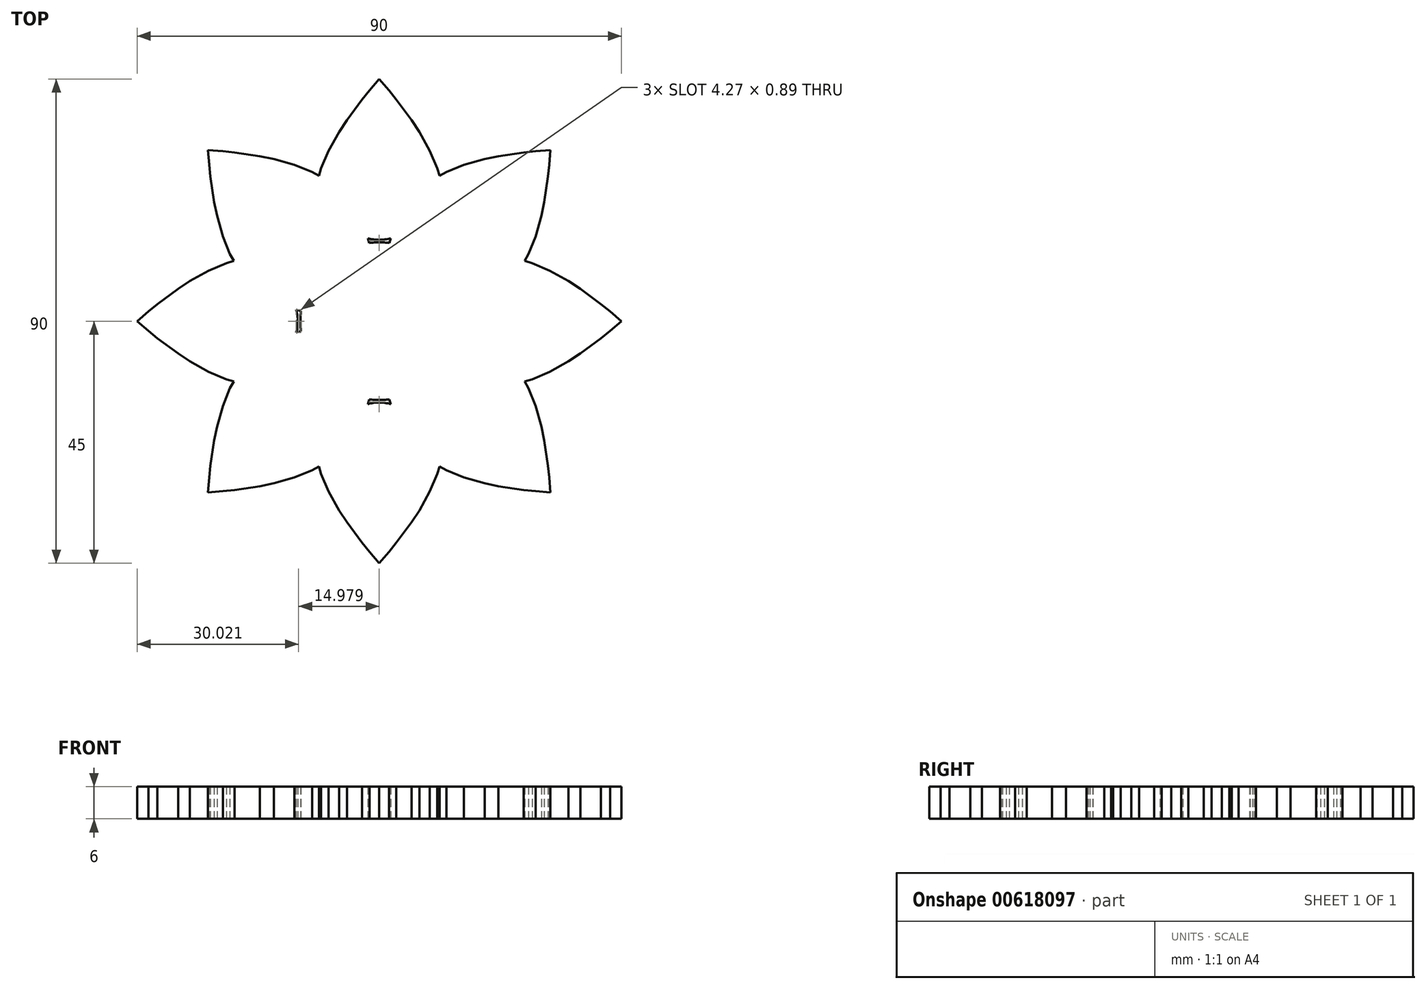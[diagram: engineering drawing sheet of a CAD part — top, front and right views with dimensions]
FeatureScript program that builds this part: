
annotation { "Feature Type Name" : "Feature", "Feature Type Description" : "" }
export const myFeature = defineFeature(function(context is Context, id is Id, definition is map)
    precondition{}
    {
        {
            var Q0;
            Q0=qCreatedBy(makeId("Top.planeOp"),FACE);
            var sketch = newSketch(context, id + "F0", { "sketchPlane" : qUnion([Q0])});
            skCircle(sketch, "E0", {"center": v(0, 0) * mm, "radius": 11.12 * mm});
            skCircle(sketch, "E1", {"center": v(22.72, 0) * mm, "radius": 7.6 * mm});
            skLineSegment(sketch, "E2", {"start": v(0, 0) * mm, "end": v(45, 0) * mm, "construction": true});
            skLineSegment(sketch, "E3", {"start": v(0, 0) * mm, "end": v(29.88, 51.75) * mm, "construction": true});
            skLineSegment(sketch, "E4", {"start": v(0, 0) * mm, "end": v(4, 3.29) * mm});
            skLineSegment(sketch, "E5", {"start": v(4, 3.29) * mm, "end": v(8.68, 6.96) * mm});
            skLineSegment(sketch, "E6", {"start": v(8.68, 6.96) * mm, "end": v(11.6, 8.96) * mm});
            skLineSegment(sketch, "E7", {"start": v(11.6, 8.96) * mm, "end": v(15.02, 10.78) * mm});
            skLineSegment(sketch, "E8", {"start": v(21.03, 12.1) * mm, "end": v(25.39, 11.67) * mm});
            skLineSegment(sketch, "E9", {"start": v(25.39, 11.67) * mm, "end": v(28.43, 10.8) * mm});
            skLineSegment(sketch, "E10", {"start": v(28.43, 10.8) * mm, "end": v(31.67, 9.4) * mm});
            skLineSegment(sketch, "E11", {"start": v(31.67, 9.4) * mm, "end": v(35.17, 7.45) * mm});
            skLineSegment(sketch, "E12", {"start": v(35.17, 7.45) * mm, "end": v(37.37, 6.01) * mm});
            skLineSegment(sketch, "E13", {"start": v(37.37, 6.01) * mm, "end": v(41.2, 3.18) * mm});
            skLineSegment(sketch, "E14", {"start": v(41.2, 3.18) * mm, "end": v(42.9, 1.8) * mm});
            skLineSegment(sketch, "E15", {"start": v(42.9, 1.8) * mm, "end": v(45, 0) * mm});
            skLineSegment(sketch, "E16", {"start": v(15.02, 10.78) * mm, "end": v(17.56, 11.63) * mm});
            skLineSegment(sketch, "E17", {"start": v(17.56, 11.63) * mm, "end": v(21.03, 12.1) * mm});
            skLineSegment(sketch, "E18.MirrorCS", {"start": v(11.6, -8.96) * mm, "end": v(15.02, -10.78) * mm});
            skLineSegment(sketch, "E19.MirrorCS", {"start": v(25.39, -11.67) * mm, "end": v(28.43, -10.8) * mm});
            skLineSegment(sketch, "E20.MirrorCS", {"start": v(8.68, -6.96) * mm, "end": v(11.6, -8.96) * mm});
            skLineSegment(sketch, "E21.MirrorCS", {"start": v(31.67, -9.4) * mm, "end": v(35.17, -7.45) * mm});
            skLineSegment(sketch, "E22.MirrorCS", {"start": v(41.2, -3.18) * mm, "end": v(42.9, -1.8) * mm});
            skLineSegment(sketch, "E23.MirrorCS", {"start": v(15.02, -10.78) * mm, "end": v(17.56, -11.63) * mm});
            skLineSegment(sketch, "E24.MirrorCS", {"start": v(17.56, -11.63) * mm, "end": v(21.03, -12.1) * mm});
            skLineSegment(sketch, "E25.MirrorCS", {"start": v(35.17, -7.45) * mm, "end": v(37.37, -6.01) * mm});
            skLineSegment(sketch, "E26.MirrorCS", {"start": v(42.9, -1.8) * mm, "end": v(45, 0) * mm});
            skLineSegment(sketch, "E27.MirrorCS", {"start": v(28.43, -10.8) * mm, "end": v(31.67, -9.4) * mm});
            skLineSegment(sketch, "E28.MirrorCS", {"start": v(4, -3.29) * mm, "end": v(8.68, -6.96) * mm});
            skLineSegment(sketch, "E29.MirrorCS", {"start": v(37.37, -6.01) * mm, "end": v(41.2, -3.18) * mm});
            skLineSegment(sketch, "E30.MirrorCS", {"start": v(21.03, -12.1) * mm, "end": v(25.39, -11.67) * mm});
            skLineSegment(sketch, "E31.MirrorCS", {"start": v(0, 0) * mm, "end": v(4, -3.29) * mm});
            skCircle(sketch, "E32", {"center": v(0, 0) * mm, "radius": 14.65 * mm});
            skLineSegment(sketch, "E33.1.0", {"start": v(0, 0) * mm, "end": v(31.82, 31.82) * mm, "construction": true});
            skCircle(sketch, "E33.1.2", {"center": v(16.07, 16.07) * mm, "radius": 7.6 * mm});
            skLineSegment(sketch, "E33.1.3", {"start": v(0, 0) * mm, "end": v(0.5, 5.15) * mm});
            skLineSegment(sketch, "E33.1.4", {"start": v(30.68, 22.17) * mm, "end": v(31.38, 26.88) * mm});
            skLineSegment(sketch, "E33.1.5", {"start": v(5.15, 0.5) * mm, "end": v(11.06, 1.22) * mm});
            skLineSegment(sketch, "E33.1.6", {"start": v(0.5, 5.15) * mm, "end": v(1.22, 11.06) * mm});
            skLineSegment(sketch, "E33.1.7", {"start": v(0, 0) * mm, "end": v(5.15, 0.5) * mm});
            skLineSegment(sketch, "E33.1.8", {"start": v(6.31, 23.43) * mm, "end": v(9.7, 26.2) * mm});
            skLineSegment(sketch, "E33.1.10", {"start": v(23.43, 6.31) * mm, "end": v(26.2, 9.7) * mm});
            skCircle(sketch, "E33.1.11", {"center": v(16.07, 16.07) * mm, "radius": 7.6 * mm});
            skLineSegment(sketch, "E33.1.12", {"start": v(0, 0) * mm, "end": v(31.82, 31.82) * mm, "construction": true});
            skLineSegment(sketch, "E33.1.14", {"start": v(20.65, 4.2) * mm, "end": v(23.43, 6.31) * mm});
            skLineSegment(sketch, "E33.1.15", {"start": v(12.47, 27.73) * mm, "end": v(15.75, 29.04) * mm});
            skLineSegment(sketch, "E33.1.16", {"start": v(3, 18.24) * mm, "end": v(4.2, 20.65) * mm});
            skLineSegment(sketch, "E33.1.17", {"start": v(4.2, 20.65) * mm, "end": v(6.31, 23.43) * mm});
            skLineSegment(sketch, "E33.1.18", {"start": v(29.04, 15.75) * mm, "end": v(30.14, 19.6) * mm});
            skLineSegment(sketch, "E33.1.19", {"start": v(31.6, 29.06) * mm, "end": v(31.82, 31.82) * mm});
            skLineSegment(sketch, "E33.1.20", {"start": v(15.75, 29.04) * mm, "end": v(19.6, 30.14) * mm});
            skLineSegment(sketch, "E33.1.21", {"start": v(30.14, 19.6) * mm, "end": v(30.68, 22.17) * mm});
            skLineSegment(sketch, "E33.1.22", {"start": v(1.86, 14.53) * mm, "end": v(3, 18.24) * mm});
            skCircle(sketch, "E33.1.23", {"center": v(16.07, 16.07) * mm, "radius": 7.6 * mm});
            skLineSegment(sketch, "E33.1.24", {"start": v(22.17, 30.68) * mm, "end": v(26.88, 31.38) * mm});
            skLineSegment(sketch, "E33.1.25", {"start": v(31.38, 26.88) * mm, "end": v(31.6, 29.06) * mm});
            skLineSegment(sketch, "E33.1.26", {"start": v(19.6, 30.14) * mm, "end": v(22.17, 30.68) * mm});
            skLineSegment(sketch, "E33.1.27", {"start": v(18.24, 3) * mm, "end": v(20.65, 4.2) * mm});
            skLineSegment(sketch, "E33.1.28", {"start": v(11.06, 1.22) * mm, "end": v(14.53, 1.86) * mm});
            skLineSegment(sketch, "E33.1.29", {"start": v(14.53, 1.86) * mm, "end": v(18.24, 3) * mm});
            skLineSegment(sketch, "E33.1.30", {"start": v(0, 0) * mm, "end": v(31.82, 31.82) * mm, "construction": true});
            skLineSegment(sketch, "E33.1.31", {"start": v(1.22, 11.06) * mm, "end": v(1.86, 14.53) * mm});
            skLineSegment(sketch, "E33.1.32", {"start": v(27.73, 12.47) * mm, "end": v(29.04, 15.75) * mm});
            skLineSegment(sketch, "E33.1.33", {"start": v(9.7, 26.2) * mm, "end": v(12.47, 27.73) * mm});
            skLineSegment(sketch, "E33.1.34", {"start": v(26.88, 31.38) * mm, "end": v(29.06, 31.6) * mm});
            skLineSegment(sketch, "E33.1.35", {"start": v(26.2, 9.7) * mm, "end": v(27.73, 12.47) * mm});
            skLineSegment(sketch, "E33.1.36", {"start": v(29.06, 31.6) * mm, "end": v(31.82, 31.82) * mm});
            skCircle(sketch, "E33.1.37", {"center": v(16.07, 16.07) * mm, "radius": 7.6 * mm});
            skLineSegment(sketch, "E33.1.38", {"start": v(0, 0) * mm, "end": v(31.82, 31.82) * mm, "construction": true});
            skLineSegment(sketch, "E33.2.0", {"start": v(0, 0) * mm, "end": v(0, 45) * mm, "construction": true});
            skCircle(sketch, "E33.2.2", {"center": v(0, 22.72) * mm, "radius": 7.6 * mm});
            skLineSegment(sketch, "E33.2.3", {"start": v(0, 0) * mm, "end": v(-3.29, 4) * mm});
            skLineSegment(sketch, "E33.2.4", {"start": v(6.01, 37.37) * mm, "end": v(3.18, 41.2) * mm});
            skLineSegment(sketch, "E33.2.5", {"start": v(3.29, 4) * mm, "end": v(6.96, 8.68) * mm});
            skLineSegment(sketch, "E33.2.6", {"start": v(-3.29, 4) * mm, "end": v(-6.96, 8.68) * mm});
            skLineSegment(sketch, "E33.2.7", {"start": v(0, 0) * mm, "end": v(3.29, 4) * mm});
            skLineSegment(sketch, "E33.2.8", {"start": v(-12.1, 21.03) * mm, "end": v(-11.67, 25.39) * mm});
            skLineSegment(sketch, "E33.2.10", {"start": v(12.1, 21.03) * mm, "end": v(11.67, 25.39) * mm});
            skCircle(sketch, "E33.2.11", {"center": v(0, 22.72) * mm, "radius": 7.6 * mm});
            skLineSegment(sketch, "E33.2.12", {"start": v(0, 0) * mm, "end": v(0, 45) * mm, "construction": true});
            skLineSegment(sketch, "E33.2.14", {"start": v(11.63, 17.56) * mm, "end": v(12.1, 21.03) * mm});
            skLineSegment(sketch, "E33.2.15", {"start": v(-10.8, 28.43) * mm, "end": v(-9.4, 31.67) * mm});
            skLineSegment(sketch, "E33.2.16", {"start": v(-10.78, 15.02) * mm, "end": v(-11.63, 17.56) * mm});
            skLineSegment(sketch, "E33.2.17", {"start": v(-11.63, 17.56) * mm, "end": v(-12.1, 21.03) * mm});
            skLineSegment(sketch, "E33.2.18", {"start": v(9.4, 31.67) * mm, "end": v(7.45, 35.17) * mm});
            skLineSegment(sketch, "E33.2.19", {"start": v(1.8, 42.9) * mm, "end": v(0, 45) * mm});
            skLineSegment(sketch, "E33.2.20", {"start": v(-9.4, 31.67) * mm, "end": v(-7.45, 35.17) * mm});
            skLineSegment(sketch, "E33.2.21", {"start": v(7.45, 35.17) * mm, "end": v(6.01, 37.37) * mm});
            skLineSegment(sketch, "E33.2.22", {"start": v(-8.96, 11.6) * mm, "end": v(-10.78, 15.02) * mm});
            skCircle(sketch, "E33.2.23", {"center": v(0, 22.72) * mm, "radius": 7.6 * mm});
            skLineSegment(sketch, "E33.2.24", {"start": v(-6.01, 37.37) * mm, "end": v(-3.18, 41.2) * mm});
            skLineSegment(sketch, "E33.2.25", {"start": v(3.18, 41.2) * mm, "end": v(1.8, 42.9) * mm});
            skLineSegment(sketch, "E33.2.26", {"start": v(-7.45, 35.17) * mm, "end": v(-6.01, 37.37) * mm});
            skLineSegment(sketch, "E33.2.27", {"start": v(10.78, 15.02) * mm, "end": v(11.63, 17.56) * mm});
            skLineSegment(sketch, "E33.2.28", {"start": v(6.96, 8.68) * mm, "end": v(8.96, 11.6) * mm});
            skLineSegment(sketch, "E33.2.29", {"start": v(8.96, 11.6) * mm, "end": v(10.78, 15.02) * mm});
            skLineSegment(sketch, "E33.2.30", {"start": v(0, 0) * mm, "end": v(0, 45) * mm, "construction": true});
            skLineSegment(sketch, "E33.2.31", {"start": v(-6.96, 8.68) * mm, "end": v(-8.96, 11.6) * mm});
            skLineSegment(sketch, "E33.2.32", {"start": v(10.8, 28.43) * mm, "end": v(9.4, 31.67) * mm});
            skLineSegment(sketch, "E33.2.33", {"start": v(-11.67, 25.39) * mm, "end": v(-10.8, 28.43) * mm});
            skLineSegment(sketch, "E33.2.34", {"start": v(-3.18, 41.2) * mm, "end": v(-1.8, 42.9) * mm});
            skLineSegment(sketch, "E33.2.35", {"start": v(11.67, 25.39) * mm, "end": v(10.8, 28.43) * mm});
            skLineSegment(sketch, "E33.2.36", {"start": v(-1.8, 42.9) * mm, "end": v(0, 45) * mm});
            skCircle(sketch, "E33.2.37", {"center": v(0, 22.72) * mm, "radius": 7.6 * mm});
            skLineSegment(sketch, "E33.2.38", {"start": v(0, 0) * mm, "end": v(0, 45) * mm, "construction": true});
            skCircle(sketch, "E34.5.3.0", {"center": v(-16.07, 16.07) * mm, "radius": 7.6 * mm});
            skLineSegment(sketch, "E34.7.3.0", {"start": v(0, 0) * mm, "end": v(-5.15, 0.5) * mm});
            skLineSegment(sketch, "E34.10.3.0", {"start": v(-22.17, 30.68) * mm, "end": v(-26.88, 31.38) * mm});
            skLineSegment(sketch, "E34.13.3.0", {"start": v(-0.5, 5.15) * mm, "end": v(-1.22, 11.06) * mm});
            skLineSegment(sketch, "E34.14.3.0", {"start": v(0, 0) * mm, "end": v(-31.82, 31.82) * mm, "construction": true});
            skLineSegment(sketch, "E34.16.3.0", {"start": v(-5.15, 0.5) * mm, "end": v(-11.06, 1.22) * mm});
            skLineSegment(sketch, "E34.19.3.0", {"start": v(0, 0) * mm, "end": v(-0.5, 5.15) * mm});
            skLineSegment(sketch, "E34.22.3.0", {"start": v(-23.43, 6.31) * mm, "end": v(-26.2, 9.7) * mm});
            skLineSegment(sketch, "E34.27.3.0", {"start": v(-6.31, 23.43) * mm, "end": v(-9.7, 26.2) * mm});
            skCircle(sketch, "E34.30.3.0", {"center": v(-16.07, 16.07) * mm, "radius": 7.6 * mm});
            skLineSegment(sketch, "E34.32.3.0", {"start": v(0, 0) * mm, "end": v(-31.82, 31.82) * mm, "construction": true});
            skLineSegment(sketch, "E34.37.3.0", {"start": v(-4.2, 20.65) * mm, "end": v(-6.31, 23.43) * mm});
            skLineSegment(sketch, "E34.40.3.0", {"start": v(-27.73, 12.47) * mm, "end": v(-29.04, 15.75) * mm});
            skLineSegment(sketch, "E34.43.3.0", {"start": v(-18.24, 3) * mm, "end": v(-20.65, 4.2) * mm});
            skLineSegment(sketch, "E34.46.3.0", {"start": v(-20.65, 4.2) * mm, "end": v(-23.43, 6.31) * mm});
            skLineSegment(sketch, "E34.49.3.0", {"start": v(-15.75, 29.04) * mm, "end": v(-19.6, 30.14) * mm});
            skLineSegment(sketch, "E34.52.3.0", {"start": v(-29.06, 31.6) * mm, "end": v(-31.82, 31.82) * mm});
            skLineSegment(sketch, "E34.55.3.0", {"start": v(-29.04, 15.75) * mm, "end": v(-30.14, 19.6) * mm});
            skLineSegment(sketch, "E34.58.3.0", {"start": v(-19.6, 30.14) * mm, "end": v(-22.17, 30.68) * mm});
            skLineSegment(sketch, "E34.61.3.0", {"start": v(-14.53, 1.86) * mm, "end": v(-18.24, 3) * mm});
            skCircle(sketch, "E34.64.3.0", {"center": v(-16.07, 16.07) * mm, "radius": 7.6 * mm});
            skLineSegment(sketch, "E34.66.3.0", {"start": v(-30.68, 22.17) * mm, "end": v(-31.38, 26.88) * mm});
            skLineSegment(sketch, "E34.69.3.0", {"start": v(-26.88, 31.38) * mm, "end": v(-29.06, 31.6) * mm});
            skLineSegment(sketch, "E34.72.3.0", {"start": v(-30.14, 19.6) * mm, "end": v(-30.68, 22.17) * mm});
            skLineSegment(sketch, "E34.75.3.0", {"start": v(-3, 18.24) * mm, "end": v(-4.2, 20.65) * mm});
            skLineSegment(sketch, "E34.78.3.0", {"start": v(-1.22, 11.06) * mm, "end": v(-1.86, 14.53) * mm});
            skLineSegment(sketch, "E34.81.3.0", {"start": v(-1.86, 14.53) * mm, "end": v(-3, 18.24) * mm});
            skLineSegment(sketch, "E34.84.3.0", {"start": v(0, 0) * mm, "end": v(-31.82, 31.82) * mm, "construction": true});
            skLineSegment(sketch, "E34.87.3.0", {"start": v(-11.06, 1.22) * mm, "end": v(-14.53, 1.86) * mm});
            skLineSegment(sketch, "E34.90.3.0", {"start": v(-12.47, 27.73) * mm, "end": v(-15.75, 29.04) * mm});
            skLineSegment(sketch, "E34.93.3.0", {"start": v(-26.2, 9.7) * mm, "end": v(-27.73, 12.47) * mm});
            skLineSegment(sketch, "E34.96.3.0", {"start": v(-31.38, 26.88) * mm, "end": v(-31.6, 29.06) * mm});
            skLineSegment(sketch, "E34.99.3.0", {"start": v(-9.7, 26.2) * mm, "end": v(-12.47, 27.73) * mm});
            skLineSegment(sketch, "E34.102.3.0", {"start": v(-31.6, 29.06) * mm, "end": v(-31.82, 31.82) * mm});
            skCircle(sketch, "E34.105.3.0", {"center": v(-16.07, 16.07) * mm, "radius": 7.6 * mm});
            skLineSegment(sketch, "E34.107.3.0", {"start": v(0, 0) * mm, "end": v(-31.82, 31.82) * mm, "construction": true});
            skCircle(sketch, "E34.5.4.0", {"center": v(-22.72, 0) * mm, "radius": 7.6 * mm});
            skLineSegment(sketch, "E34.7.4.0", {"start": v(0, 0) * mm, "end": v(-4, -3.29) * mm});
            skLineSegment(sketch, "E34.10.4.0", {"start": v(-37.37, 6.01) * mm, "end": v(-41.2, 3.18) * mm});
            skLineSegment(sketch, "E34.13.4.0", {"start": v(-4, 3.29) * mm, "end": v(-8.68, 6.96) * mm});
            skLineSegment(sketch, "E34.14.4.0", {"start": v(0, 0) * mm, "end": v(-45, 0) * mm, "construction": true});
            skLineSegment(sketch, "E34.16.4.0", {"start": v(-4, -3.29) * mm, "end": v(-8.68, -6.96) * mm});
            skLineSegment(sketch, "E34.19.4.0", {"start": v(0, 0) * mm, "end": v(-4, 3.29) * mm});
            skLineSegment(sketch, "E34.22.4.0", {"start": v(-21.03, -12.1) * mm, "end": v(-25.39, -11.67) * mm});
            skLineSegment(sketch, "E34.27.4.0", {"start": v(-21.03, 12.1) * mm, "end": v(-25.39, 11.67) * mm});
            skCircle(sketch, "E34.30.4.0", {"center": v(-22.72, 0) * mm, "radius": 7.6 * mm});
            skLineSegment(sketch, "E34.32.4.0", {"start": v(0, 0) * mm, "end": v(-45, 0) * mm, "construction": true});
            skLineSegment(sketch, "E34.37.4.0", {"start": v(-17.56, 11.63) * mm, "end": v(-21.03, 12.1) * mm});
            skLineSegment(sketch, "E34.40.4.0", {"start": v(-28.43, -10.8) * mm, "end": v(-31.67, -9.4) * mm});
            skLineSegment(sketch, "E34.43.4.0", {"start": v(-15.02, -10.78) * mm, "end": v(-17.56, -11.63) * mm});
            skLineSegment(sketch, "E34.46.4.0", {"start": v(-17.56, -11.63) * mm, "end": v(-21.03, -12.1) * mm});
            skLineSegment(sketch, "E34.49.4.0", {"start": v(-31.67, 9.4) * mm, "end": v(-35.17, 7.45) * mm});
            skLineSegment(sketch, "E34.52.4.0", {"start": v(-42.9, 1.8) * mm, "end": v(-45, 0) * mm});
            skLineSegment(sketch, "E34.55.4.0", {"start": v(-31.67, -9.4) * mm, "end": v(-35.17, -7.45) * mm});
            skLineSegment(sketch, "E34.58.4.0", {"start": v(-35.17, 7.45) * mm, "end": v(-37.37, 6.01) * mm});
            skLineSegment(sketch, "E34.61.4.0", {"start": v(-11.6, -8.96) * mm, "end": v(-15.02, -10.78) * mm});
            skCircle(sketch, "E34.64.4.0", {"center": v(-22.72, 0) * mm, "radius": 7.6 * mm});
            skLineSegment(sketch, "E34.66.4.0", {"start": v(-37.37, -6.01) * mm, "end": v(-41.2, -3.18) * mm});
            skLineSegment(sketch, "E34.69.4.0", {"start": v(-41.2, 3.18) * mm, "end": v(-42.9, 1.8) * mm});
            skLineSegment(sketch, "E34.72.4.0", {"start": v(-35.17, -7.45) * mm, "end": v(-37.37, -6.01) * mm});
            skLineSegment(sketch, "E34.75.4.0", {"start": v(-15.02, 10.78) * mm, "end": v(-17.56, 11.63) * mm});
            skLineSegment(sketch, "E34.78.4.0", {"start": v(-8.68, 6.96) * mm, "end": v(-11.6, 8.96) * mm});
            skLineSegment(sketch, "E34.81.4.0", {"start": v(-11.6, 8.96) * mm, "end": v(-15.02, 10.78) * mm});
            skLineSegment(sketch, "E34.84.4.0", {"start": v(0, 0) * mm, "end": v(-45, 0) * mm, "construction": true});
            skLineSegment(sketch, "E34.87.4.0", {"start": v(-8.68, -6.96) * mm, "end": v(-11.6, -8.96) * mm});
            skLineSegment(sketch, "E34.90.4.0", {"start": v(-28.43, 10.8) * mm, "end": v(-31.67, 9.4) * mm});
            skLineSegment(sketch, "E34.93.4.0", {"start": v(-25.39, -11.67) * mm, "end": v(-28.43, -10.8) * mm});
            skLineSegment(sketch, "E34.96.4.0", {"start": v(-41.2, -3.18) * mm, "end": v(-42.9, -1.8) * mm});
            skLineSegment(sketch, "E34.99.4.0", {"start": v(-25.39, 11.67) * mm, "end": v(-28.43, 10.8) * mm});
            skLineSegment(sketch, "E34.102.4.0", {"start": v(-42.9, -1.8) * mm, "end": v(-45, 0) * mm});
            skCircle(sketch, "E34.105.4.0", {"center": v(-22.72, 0) * mm, "radius": 7.6 * mm});
            skLineSegment(sketch, "E34.107.4.0", {"start": v(0, 0) * mm, "end": v(-45, 0) * mm, "construction": true});
            skCircle(sketch, "E34.5.5.0", {"center": v(-16.07, -16.07) * mm, "radius": 7.6 * mm});
            skLineSegment(sketch, "E34.7.5.0", {"start": v(0, 0) * mm, "end": v(-0.5, -5.15) * mm});
            skLineSegment(sketch, "E34.10.5.0", {"start": v(-30.68, -22.17) * mm, "end": v(-31.38, -26.88) * mm});
            skLineSegment(sketch, "E34.13.5.0", {"start": v(-5.15, -0.5) * mm, "end": v(-11.06, -1.22) * mm});
            skLineSegment(sketch, "E34.14.5.0", {"start": v(0, 0) * mm, "end": v(-31.82, -31.82) * mm, "construction": true});
            skLineSegment(sketch, "E34.16.5.0", {"start": v(-0.5, -5.15) * mm, "end": v(-1.22, -11.06) * mm});
            skLineSegment(sketch, "E34.19.5.0", {"start": v(0, 0) * mm, "end": v(-5.15, -0.5) * mm});
            skLineSegment(sketch, "E34.22.5.0", {"start": v(-6.31, -23.43) * mm, "end": v(-9.7, -26.2) * mm});
            skLineSegment(sketch, "E34.27.5.0", {"start": v(-23.43, -6.31) * mm, "end": v(-26.2, -9.7) * mm});
            skCircle(sketch, "E34.30.5.0", {"center": v(-16.07, -16.07) * mm, "radius": 7.6 * mm});
            skLineSegment(sketch, "E34.32.5.0", {"start": v(0, 0) * mm, "end": v(-31.82, -31.82) * mm, "construction": true});
            skLineSegment(sketch, "E34.37.5.0", {"start": v(-20.65, -4.2) * mm, "end": v(-23.43, -6.31) * mm});
            skLineSegment(sketch, "E34.40.5.0", {"start": v(-12.47, -27.73) * mm, "end": v(-15.75, -29.04) * mm});
            skLineSegment(sketch, "E34.43.5.0", {"start": v(-3, -18.24) * mm, "end": v(-4.2, -20.65) * mm});
            skLineSegment(sketch, "E34.46.5.0", {"start": v(-4.2, -20.65) * mm, "end": v(-6.31, -23.43) * mm});
            skLineSegment(sketch, "E34.49.5.0", {"start": v(-29.04, -15.75) * mm, "end": v(-30.14, -19.6) * mm});
            skLineSegment(sketch, "E34.52.5.0", {"start": v(-31.6, -29.06) * mm, "end": v(-31.82, -31.82) * mm});
            skLineSegment(sketch, "E34.55.5.0", {"start": v(-15.75, -29.04) * mm, "end": v(-19.6, -30.14) * mm});
            skLineSegment(sketch, "E34.58.5.0", {"start": v(-30.14, -19.6) * mm, "end": v(-30.68, -22.17) * mm});
            skLineSegment(sketch, "E34.61.5.0", {"start": v(-1.86, -14.53) * mm, "end": v(-3, -18.24) * mm});
            skCircle(sketch, "E34.64.5.0", {"center": v(-16.07, -16.07) * mm, "radius": 7.6 * mm});
            skLineSegment(sketch, "E34.66.5.0", {"start": v(-22.17, -30.68) * mm, "end": v(-26.88, -31.38) * mm});
            skLineSegment(sketch, "E34.69.5.0", {"start": v(-31.38, -26.88) * mm, "end": v(-31.6, -29.06) * mm});
            skLineSegment(sketch, "E34.72.5.0", {"start": v(-19.6, -30.14) * mm, "end": v(-22.17, -30.68) * mm});
            skLineSegment(sketch, "E34.75.5.0", {"start": v(-18.24, -3) * mm, "end": v(-20.65, -4.2) * mm});
            skLineSegment(sketch, "E34.78.5.0", {"start": v(-11.06, -1.22) * mm, "end": v(-14.53, -1.86) * mm});
            skLineSegment(sketch, "E34.81.5.0", {"start": v(-14.53, -1.86) * mm, "end": v(-18.24, -3) * mm});
            skLineSegment(sketch, "E34.84.5.0", {"start": v(0, 0) * mm, "end": v(-31.82, -31.82) * mm, "construction": true});
            skLineSegment(sketch, "E34.87.5.0", {"start": v(-1.22, -11.06) * mm, "end": v(-1.86, -14.53) * mm});
            skLineSegment(sketch, "E34.90.5.0", {"start": v(-27.73, -12.47) * mm, "end": v(-29.04, -15.75) * mm});
            skLineSegment(sketch, "E34.93.5.0", {"start": v(-9.7, -26.2) * mm, "end": v(-12.47, -27.73) * mm});
            skLineSegment(sketch, "E34.96.5.0", {"start": v(-26.88, -31.38) * mm, "end": v(-29.06, -31.6) * mm});
            skLineSegment(sketch, "E34.99.5.0", {"start": v(-26.2, -9.7) * mm, "end": v(-27.73, -12.47) * mm});
            skLineSegment(sketch, "E34.102.5.0", {"start": v(-29.06, -31.6) * mm, "end": v(-31.82, -31.82) * mm});
            skCircle(sketch, "E34.105.5.0", {"center": v(-16.07, -16.07) * mm, "radius": 7.6 * mm});
            skLineSegment(sketch, "E34.107.5.0", {"start": v(0, 0) * mm, "end": v(-31.82, -31.82) * mm, "construction": true});
            skCircle(sketch, "E34.5.6.0", {"center": v(0, -22.72) * mm, "radius": 7.6 * mm});
            skLineSegment(sketch, "E34.7.6.0", {"start": v(0, 0) * mm, "end": v(3.29, -4) * mm});
            skLineSegment(sketch, "E34.10.6.0", {"start": v(-6.01, -37.37) * mm, "end": v(-3.18, -41.2) * mm});
            skLineSegment(sketch, "E34.13.6.0", {"start": v(-3.29, -4) * mm, "end": v(-6.96, -8.68) * mm});
            skLineSegment(sketch, "E34.14.6.0", {"start": v(0, 0) * mm, "end": v(0, -45) * mm, "construction": true});
            skLineSegment(sketch, "E34.16.6.0", {"start": v(3.29, -4) * mm, "end": v(6.96, -8.68) * mm});
            skLineSegment(sketch, "E34.19.6.0", {"start": v(0, 0) * mm, "end": v(-3.29, -4) * mm});
            skLineSegment(sketch, "E34.22.6.0", {"start": v(12.1, -21.03) * mm, "end": v(11.67, -25.39) * mm});
            skLineSegment(sketch, "E34.27.6.0", {"start": v(-12.1, -21.03) * mm, "end": v(-11.67, -25.39) * mm});
            skCircle(sketch, "E34.30.6.0", {"center": v(0, -22.72) * mm, "radius": 7.6 * mm});
            skLineSegment(sketch, "E34.32.6.0", {"start": v(0, 0) * mm, "end": v(0, -45) * mm, "construction": true});
            skLineSegment(sketch, "E34.37.6.0", {"start": v(-11.63, -17.56) * mm, "end": v(-12.1, -21.03) * mm});
            skLineSegment(sketch, "E34.40.6.0", {"start": v(10.8, -28.43) * mm, "end": v(9.4, -31.67) * mm});
            skLineSegment(sketch, "E34.43.6.0", {"start": v(10.78, -15.02) * mm, "end": v(11.63, -17.56) * mm});
            skLineSegment(sketch, "E34.46.6.0", {"start": v(11.63, -17.56) * mm, "end": v(12.1, -21.03) * mm});
            skLineSegment(sketch, "E34.49.6.0", {"start": v(-9.4, -31.67) * mm, "end": v(-7.45, -35.17) * mm});
            skLineSegment(sketch, "E34.52.6.0", {"start": v(-1.8, -42.9) * mm, "end": v(0, -45) * mm});
            skLineSegment(sketch, "E34.55.6.0", {"start": v(9.4, -31.67) * mm, "end": v(7.45, -35.17) * mm});
            skLineSegment(sketch, "E34.58.6.0", {"start": v(-7.45, -35.17) * mm, "end": v(-6.01, -37.37) * mm});
            skLineSegment(sketch, "E34.61.6.0", {"start": v(8.96, -11.6) * mm, "end": v(10.78, -15.02) * mm});
            skCircle(sketch, "E34.64.6.0", {"center": v(0, -22.72) * mm, "radius": 7.6 * mm});
            skLineSegment(sketch, "E34.66.6.0", {"start": v(6.01, -37.37) * mm, "end": v(3.18, -41.2) * mm});
            skLineSegment(sketch, "E34.69.6.0", {"start": v(-3.18, -41.2) * mm, "end": v(-1.8, -42.9) * mm});
            skLineSegment(sketch, "E34.72.6.0", {"start": v(7.45, -35.17) * mm, "end": v(6.01, -37.37) * mm});
            skLineSegment(sketch, "E34.75.6.0", {"start": v(-10.78, -15.02) * mm, "end": v(-11.63, -17.56) * mm});
            skLineSegment(sketch, "E34.78.6.0", {"start": v(-6.96, -8.68) * mm, "end": v(-8.96, -11.6) * mm});
            skLineSegment(sketch, "E34.81.6.0", {"start": v(-8.96, -11.6) * mm, "end": v(-10.78, -15.02) * mm});
            skLineSegment(sketch, "E34.84.6.0", {"start": v(0, 0) * mm, "end": v(0, -45) * mm, "construction": true});
            skLineSegment(sketch, "E34.87.6.0", {"start": v(6.96, -8.68) * mm, "end": v(8.96, -11.6) * mm});
            skLineSegment(sketch, "E34.90.6.0", {"start": v(-10.8, -28.43) * mm, "end": v(-9.4, -31.67) * mm});
            skLineSegment(sketch, "E34.93.6.0", {"start": v(11.67, -25.39) * mm, "end": v(10.8, -28.43) * mm});
            skLineSegment(sketch, "E34.96.6.0", {"start": v(3.18, -41.2) * mm, "end": v(1.8, -42.9) * mm});
            skLineSegment(sketch, "E34.99.6.0", {"start": v(-11.67, -25.39) * mm, "end": v(-10.8, -28.43) * mm});
            skLineSegment(sketch, "E34.102.6.0", {"start": v(1.8, -42.9) * mm, "end": v(0, -45) * mm});
            skCircle(sketch, "E34.105.6.0", {"center": v(0, -22.72) * mm, "radius": 7.6 * mm});
            skLineSegment(sketch, "E34.107.6.0", {"start": v(0, 0) * mm, "end": v(0, -45) * mm, "construction": true});
            skCircle(sketch, "E34.5.7.0", {"center": v(16.07, -16.07) * mm, "radius": 7.6 * mm});
            skLineSegment(sketch, "E34.7.7.0", {"start": v(0, 0) * mm, "end": v(5.15, -0.5) * mm});
            skLineSegment(sketch, "E34.10.7.0", {"start": v(22.17, -30.68) * mm, "end": v(26.88, -31.38) * mm});
            skLineSegment(sketch, "E34.13.7.0", {"start": v(0.5, -5.15) * mm, "end": v(1.22, -11.06) * mm});
            skLineSegment(sketch, "E34.14.7.0", {"start": v(0, 0) * mm, "end": v(31.82, -31.82) * mm, "construction": true});
            skLineSegment(sketch, "E34.16.7.0", {"start": v(5.15, -0.5) * mm, "end": v(11.06, -1.22) * mm});
            skLineSegment(sketch, "E34.19.7.0", {"start": v(0, 0) * mm, "end": v(0.5, -5.15) * mm});
            skLineSegment(sketch, "E34.22.7.0", {"start": v(23.43, -6.31) * mm, "end": v(26.2, -9.7) * mm});
            skLineSegment(sketch, "E34.27.7.0", {"start": v(6.31, -23.43) * mm, "end": v(9.7, -26.2) * mm});
            skCircle(sketch, "E34.30.7.0", {"center": v(16.07, -16.07) * mm, "radius": 7.6 * mm});
            skLineSegment(sketch, "E34.32.7.0", {"start": v(0, 0) * mm, "end": v(31.82, -31.82) * mm, "construction": true});
            skLineSegment(sketch, "E34.37.7.0", {"start": v(4.2, -20.65) * mm, "end": v(6.31, -23.43) * mm});
            skLineSegment(sketch, "E34.40.7.0", {"start": v(27.73, -12.47) * mm, "end": v(29.04, -15.75) * mm});
            skLineSegment(sketch, "E34.43.7.0", {"start": v(18.24, -3) * mm, "end": v(20.65, -4.2) * mm});
            skLineSegment(sketch, "E34.46.7.0", {"start": v(20.65, -4.2) * mm, "end": v(23.43, -6.31) * mm});
            skLineSegment(sketch, "E34.49.7.0", {"start": v(15.75, -29.04) * mm, "end": v(19.6, -30.14) * mm});
            skLineSegment(sketch, "E34.52.7.0", {"start": v(29.06, -31.6) * mm, "end": v(31.82, -31.82) * mm});
            skLineSegment(sketch, "E34.55.7.0", {"start": v(29.04, -15.75) * mm, "end": v(30.14, -19.6) * mm});
            skLineSegment(sketch, "E34.58.7.0", {"start": v(19.6, -30.14) * mm, "end": v(22.17, -30.68) * mm});
            skLineSegment(sketch, "E34.61.7.0", {"start": v(14.53, -1.86) * mm, "end": v(18.24, -3) * mm});
            skCircle(sketch, "E34.64.7.0", {"center": v(16.07, -16.07) * mm, "radius": 7.6 * mm});
            skLineSegment(sketch, "E34.66.7.0", {"start": v(30.68, -22.17) * mm, "end": v(31.38, -26.88) * mm});
            skLineSegment(sketch, "E34.69.7.0", {"start": v(26.88, -31.38) * mm, "end": v(29.06, -31.6) * mm});
            skLineSegment(sketch, "E34.72.7.0", {"start": v(30.14, -19.6) * mm, "end": v(30.68, -22.17) * mm});
            skLineSegment(sketch, "E34.75.7.0", {"start": v(3, -18.24) * mm, "end": v(4.2, -20.65) * mm});
            skLineSegment(sketch, "E34.78.7.0", {"start": v(1.22, -11.06) * mm, "end": v(1.86, -14.53) * mm});
            skLineSegment(sketch, "E34.81.7.0", {"start": v(1.86, -14.53) * mm, "end": v(3, -18.24) * mm});
            skLineSegment(sketch, "E34.84.7.0", {"start": v(0, 0) * mm, "end": v(31.82, -31.82) * mm, "construction": true});
            skLineSegment(sketch, "E34.87.7.0", {"start": v(11.06, -1.22) * mm, "end": v(14.53, -1.86) * mm});
            skLineSegment(sketch, "E34.90.7.0", {"start": v(12.47, -27.73) * mm, "end": v(15.75, -29.04) * mm});
            skLineSegment(sketch, "E34.93.7.0", {"start": v(26.2, -9.7) * mm, "end": v(27.73, -12.47) * mm});
            skLineSegment(sketch, "E34.96.7.0", {"start": v(31.38, -26.88) * mm, "end": v(31.6, -29.06) * mm});
            skLineSegment(sketch, "E34.99.7.0", {"start": v(9.7, -26.2) * mm, "end": v(12.47, -27.73) * mm});
            skLineSegment(sketch, "E34.102.7.0", {"start": v(31.6, -29.06) * mm, "end": v(31.82, -31.82) * mm});
            skCircle(sketch, "E34.105.7.0", {"center": v(16.07, -16.07) * mm, "radius": 7.6 * mm});
            skLineSegment(sketch, "E34.107.7.0", {"start": v(0, 0) * mm, "end": v(31.82, -31.82) * mm, "construction": true});
            skSolve(sketch);
        }
        {
            var Q0;
            Q0=makeQuery(id+"F0.imprint","IMPRINT",FACE,{"disambiguationData":[TD([[makeQuery(id+"F0.imprint","IMPRINT",EDGE,{"derivedFrom":sQuery(id+"F0.wireOp",EDGE,"E34.10.7.0")}),1.0]])]});
            var Q1;
            Q1=makeQuery(id+"F0.imprint","IMPRINT",FACE,{"disambiguationData":[TD([[makeQuery(id+"F0.imprint","IMPRINT",EDGE,{"derivedFrom":sQuery(id+"F0.wireOp",EDGE,"E33.1.4")}),1.0]])]});
            var Q2;
            {var subQ7=sQuery(id+"F0.wireOp",EDGE,"E10");Q2=makeQuery(id+"F0.imprint","IMPRINT",FACE,{"disambiguationData":[TD([[makeQuery(id+"F0.imprint","IMPRINT",EDGE,{"derivedFrom":subQ7}),-1.0]])]});}
            var Q3;
            {var subQ5=sQuery(id+"F0.wireOp",EDGE,"E33.1.33");var subQ6=sQuery(id+"F0.wireOp",EDGE,"E33.1.8");var subQ7=makeQuery(id+"F0.imprint","INTERSECT",VERTEX,{"derivedFrom":[subQ6,subQ5]});Q3=makeQuery(id+"F0.imprint","IMPRINT",FACE,{"disambiguationData":[TD([[makeQuery(id+"F0.imprint","IMPRINT",EDGE,{"disambiguationData":[TD([[subQ7,1.0]])],"derivedFrom":subQ6}),-1.0]])]});}
            var Q4;
            {var subQ1=sQuery(id+"F0.wireOp",EDGE,"E34.43.4.0");Q4=makeQuery(id+"F0.imprint","IMPRINT",FACE,{"disambiguationData":[TD([[makeQuery(id+"F0.imprint","IMPRINT",EDGE,{"derivedFrom":subQ1}),1.0]])]});}
            var Q5;
            {var subQ5=sQuery(id+"F0.wireOp",EDGE,"E34.93.3.0");var subQ6=sQuery(id+"F0.wireOp",EDGE,"E34.22.3.0");var subQ7=makeQuery(id+"F0.imprint","INTERSECT",VERTEX,{"derivedFrom":[subQ6,subQ5]});Q5=makeQuery(id+"F0.imprint","IMPRINT",FACE,{"disambiguationData":[TD([[makeQuery(id+"F0.imprint","IMPRINT",EDGE,{"disambiguationData":[TD([[subQ7,1.0]])],"derivedFrom":subQ6}),-1.0]])]});}
            var Q6;
            {var subQ1=sQuery(id+"F0.wireOp",EDGE,"E34.43.5.0");Q6=makeQuery(id+"F0.imprint","IMPRINT",FACE,{"disambiguationData":[TD([[makeQuery(id+"F0.imprint","IMPRINT",EDGE,{"derivedFrom":subQ1}),1.0]])]});}
            var Q7;
            {var subQ5=sQuery(id+"F0.wireOp",EDGE,"E34.93.6.0");var subQ6=sQuery(id+"F0.wireOp",EDGE,"E34.22.6.0");var subQ7=makeQuery(id+"F0.imprint","INTERSECT",VERTEX,{"derivedFrom":[subQ6,subQ5]});Q7=makeQuery(id+"F0.imprint","IMPRINT",FACE,{"disambiguationData":[TD([[makeQuery(id+"F0.imprint","IMPRINT",EDGE,{"disambiguationData":[TD([[subQ7,1.0]])],"derivedFrom":subQ6}),-1.0]])]});}
            var Q8;
            {var subQ5=sQuery(id+"F0.wireOp",EDGE,"E34.93.4.0");var subQ6=sQuery(id+"F0.wireOp",EDGE,"E34.22.4.0");var subQ7=makeQuery(id+"F0.imprint","INTERSECT",VERTEX,{"derivedFrom":[subQ6,subQ5]});Q8=makeQuery(id+"F0.imprint","IMPRINT",FACE,{"disambiguationData":[TD([[makeQuery(id+"F0.imprint","IMPRINT",EDGE,{"disambiguationData":[TD([[subQ7,1.0]])],"derivedFrom":subQ6}),-1.0]])]});}
            var Q9;
            Q9=makeQuery(id+"F0.imprint","IMPRINT",FACE,{"disambiguationData":[TD([[makeQuery(id+"F0.imprint","IMPRINT",EDGE,{"derivedFrom":sQuery(id+"F0.wireOp",EDGE,"E33.2.4")}),1.0]])]});
            var Q10;
            Q10=makeQuery(id+"F0.imprint","IMPRINT",FACE,{"disambiguationData":[TD([[makeQuery(id+"F0.imprint","IMPRINT",EDGE,{"derivedFrom":sQuery(id+"F0.wireOp",EDGE,"E34.10.3.0")}),1.0]])]});
            var Q11;
            Q11=makeQuery(id+"F0.imprint","IMPRINT",FACE,{"disambiguationData":[TD([[makeQuery(id+"F0.imprint","IMPRINT",EDGE,{"derivedFrom":sQuery(id+"F0.wireOp",EDGE,"E34.10.4.0")}),1.0]])]});
            var Q12;
            {var subQ1=sQuery(id+"F0.wireOp",EDGE,"E34.43.3.0");Q12=makeQuery(id+"F0.imprint","IMPRINT",FACE,{"disambiguationData":[TD([[makeQuery(id+"F0.imprint","IMPRINT",EDGE,{"derivedFrom":subQ1}),1.0]])]});}
            var Q13;
            {var subQ0=sQuery(id+"F0.wireOp",EDGE,"E30.MirrorCS");var subQ1=sQuery(id+"F0.wireOp",EDGE,"E19.MirrorCS");var subQ2=makeQuery(id+"F0.imprint","INTERSECT",VERTEX,{"derivedFrom":[subQ1,subQ0]});Q13=makeQuery(id+"F0.imprint","IMPRINT",FACE,{"disambiguationData":[TD([[makeQuery(id+"F0.imprint","IMPRINT",EDGE,{"disambiguationData":[TD([[subQ2,-1.0]])],"derivedFrom":subQ1}),1.0]])]});}
            var Q14;
            {var subQ0=sQuery(id+"F0.wireOp",EDGE,"E9");var subQ1=sQuery(id+"F0.wireOp",EDGE,"E8");var subQ2=makeQuery(id+"F0.imprint","INTERSECT",VERTEX,{"derivedFrom":[subQ1,subQ0]});Q14=makeQuery(id+"F0.imprint","IMPRINT",FACE,{"disambiguationData":[TD([[makeQuery(id+"F0.imprint","IMPRINT",EDGE,{"disambiguationData":[TD([[subQ2,1.0]])],"derivedFrom":subQ1}),-1.0]])]});}
            var Q15;
            {var subQ1=sQuery(id+"F0.wireOp",EDGE,"E33.2.16");Q15=makeQuery(id+"F0.imprint","IMPRINT",FACE,{"disambiguationData":[TD([[makeQuery(id+"F0.imprint","IMPRINT",EDGE,{"derivedFrom":subQ1}),1.0]])]});}
            var Q16;
            Q16=makeQuery(id+"F0.imprint","IMPRINT",FACE,{"disambiguationData":[TD([[makeQuery(id+"F0.imprint","IMPRINT",EDGE,{"derivedFrom":sQuery(id+"F0.wireOp",EDGE,"E34.10.5.0")}),1.0]])]});
            var Q17;
            Q17=makeQuery(id+"F0.imprint","IMPRINT",FACE,{"disambiguationData":[TD([[makeQuery(id+"F0.imprint","IMPRINT",EDGE,{"derivedFrom":sQuery(id+"F0.wireOp",EDGE,"E34.10.6.0")}),1.0]])]});
            var Q18;
            {var subQ4=sQuery(id+"F0.wireOp",EDGE,"E16");Q18=makeQuery(id+"F0.imprint","IMPRINT",FACE,{"disambiguationData":[TD([[makeQuery(id+"F0.imprint","IMPRINT",EDGE,{"derivedFrom":subQ4}),1.0]])]});}
            var Q19;
            {var subQ0=sQuery(id+"F0.wireOp",EDGE,"E33.1.14");Q19=makeQuery(id+"F0.imprint","IMPRINT",FACE,{"disambiguationData":[TD([[makeQuery(id+"F0.imprint","IMPRINT",EDGE,{"derivedFrom":subQ0}),-1.0]])]});}
            var Q20;
            {var subQ1=sQuery(id+"F0.wireOp",EDGE,"E33.1.16");Q20=makeQuery(id+"F0.imprint","IMPRINT",FACE,{"disambiguationData":[TD([[makeQuery(id+"F0.imprint","IMPRINT",EDGE,{"derivedFrom":subQ1}),1.0]])]});}
            var Q21;
            {var subQ4=sQuery(id+"F0.wireOp",EDGE,"E23.MirrorCS");Q21=makeQuery(id+"F0.imprint","IMPRINT",FACE,{"disambiguationData":[TD([[makeQuery(id+"F0.imprint","IMPRINT",EDGE,{"derivedFrom":subQ4}),-1.0]])]});}
            var Q22;
            {var subQ4=sQuery(id+"F0.wireOp",EDGE,"E23.MirrorCS");Q22=makeQuery(id+"F0.imprint","IMPRINT",FACE,{"disambiguationData":[TD([[makeQuery(id+"F0.imprint","IMPRINT",EDGE,{"derivedFrom":subQ4}),1.0]])]});}
            var Q23;
            {var subQ0=sQuery(id+"F0.wireOp",EDGE,"E33.1.14");Q23=makeQuery(id+"F0.imprint","IMPRINT",FACE,{"disambiguationData":[TD([[makeQuery(id+"F0.imprint","IMPRINT",EDGE,{"derivedFrom":subQ0}),1.0]])]});}
            var Q24;
            {var subQ1=sQuery(id+"F0.wireOp",EDGE,"E33.1.16");Q24=makeQuery(id+"F0.imprint","IMPRINT",FACE,{"disambiguationData":[TD([[makeQuery(id+"F0.imprint","IMPRINT",EDGE,{"derivedFrom":subQ1}),-1.0]])]});}
            var Q25;
            {var subQ1=sQuery(id+"F0.wireOp",EDGE,"E34.43.7.0");Q25=makeQuery(id+"F0.imprint","IMPRINT",FACE,{"disambiguationData":[TD([[makeQuery(id+"F0.imprint","IMPRINT",EDGE,{"derivedFrom":subQ1}),-1.0]])]});}
            var Q26;
            {var subQ0=sQuery(id+"F0.wireOp",EDGE,"E33.2.14");Q26=makeQuery(id+"F0.imprint","IMPRINT",FACE,{"disambiguationData":[TD([[makeQuery(id+"F0.imprint","IMPRINT",EDGE,{"derivedFrom":subQ0}),1.0]])]});}
            var Q27;
            {var subQ0=sQuery(id+"F0.wireOp",EDGE,"E34.37.3.0");Q27=makeQuery(id+"F0.imprint","IMPRINT",FACE,{"disambiguationData":[TD([[makeQuery(id+"F0.imprint","IMPRINT",EDGE,{"derivedFrom":subQ0}),1.0]])]});}
            var Q28;
            {var subQ1=sQuery(id+"F0.wireOp",EDGE,"E34.43.3.0");Q28=makeQuery(id+"F0.imprint","IMPRINT",FACE,{"disambiguationData":[TD([[makeQuery(id+"F0.imprint","IMPRINT",EDGE,{"derivedFrom":subQ1}),-1.0]])]});}
            var Q29;
            {var subQ1=sQuery(id+"F0.wireOp",EDGE,"E34.43.4.0");Q29=makeQuery(id+"F0.imprint","IMPRINT",FACE,{"disambiguationData":[TD([[makeQuery(id+"F0.imprint","IMPRINT",EDGE,{"derivedFrom":subQ1}),-1.0]])]});}
            var Q30;
            {var subQ1=sQuery(id+"F0.wireOp",EDGE,"E34.43.5.0");Q30=makeQuery(id+"F0.imprint","IMPRINT",FACE,{"disambiguationData":[TD([[makeQuery(id+"F0.imprint","IMPRINT",EDGE,{"derivedFrom":subQ1}),-1.0]])]});}
            var Q31;
            {var subQ1=sQuery(id+"F0.wireOp",EDGE,"E34.43.6.0");Q31=makeQuery(id+"F0.imprint","IMPRINT",FACE,{"disambiguationData":[TD([[makeQuery(id+"F0.imprint","IMPRINT",EDGE,{"derivedFrom":subQ1}),-1.0]])]});}
            var Q32;
            {var subQ1=sQuery(id+"F0.wireOp",EDGE,"E34.37.7.0");Q32=makeQuery(id+"F0.imprint","IMPRINT",FACE,{"disambiguationData":[TD([[makeQuery(id+"F0.imprint","IMPRINT",EDGE,{"derivedFrom":subQ1}),1.0]])]});}
            var Q33;
            Q33=makeQuery(id+"F0.imprint","IMPRINT",FACE,{"disambiguationData":[TD([[makeQuery(id+"F0.imprint","IMPRINT",EDGE,{"derivedFrom":sQuery(id+"F0.wireOp",EDGE,"E33.1.3")}),-1.0]])]});
            var Q34;
            {var subQ4=sQuery(id+"F0.wireOp",EDGE,"E16");Q34=makeQuery(id+"F0.imprint","IMPRINT",FACE,{"disambiguationData":[TD([[makeQuery(id+"F0.imprint","IMPRINT",EDGE,{"derivedFrom":subQ4}),-1.0]])]});}
            var Q35;
            {var subQ0=sQuery(id+"F0.wireOp",EDGE,"E34.87.3.0");Q35=makeQuery(id+"F0.imprint","IMPRINT",FACE,{"disambiguationData":[TD([[makeQuery(id+"F0.imprint","IMPRINT",EDGE,{"derivedFrom":subQ0}),-1.0]])]});}
            var Q36;
            {var subQ0=sQuery(id+"F0.wireOp",EDGE,"E34.87.4.0");Q36=makeQuery(id+"F0.imprint","IMPRINT",FACE,{"disambiguationData":[TD([[makeQuery(id+"F0.imprint","IMPRINT",EDGE,{"derivedFrom":subQ0}),-1.0]])]});}
            var Q37;
            {var subQ0=sQuery(id+"F0.wireOp",EDGE,"E34.87.5.0");Q37=makeQuery(id+"F0.imprint","IMPRINT",FACE,{"disambiguationData":[TD([[makeQuery(id+"F0.imprint","IMPRINT",EDGE,{"derivedFrom":subQ0}),-1.0]])]});}
            var Q38;
            {var subQ5=sQuery(id+"F0.wireOp",EDGE,"E33.2.33");var subQ6=sQuery(id+"F0.wireOp",EDGE,"E33.2.8");var subQ7=makeQuery(id+"F0.imprint","INTERSECT",VERTEX,{"derivedFrom":[subQ6,subQ5]});Q38=makeQuery(id+"F0.imprint","IMPRINT",FACE,{"disambiguationData":[TD([[makeQuery(id+"F0.imprint","IMPRINT",EDGE,{"disambiguationData":[TD([[subQ7,1.0]])],"derivedFrom":subQ6}),-1.0]])]});}
            var Q39;
            {var subQ5=sQuery(id+"F0.wireOp",EDGE,"E34.93.5.0");var subQ6=sQuery(id+"F0.wireOp",EDGE,"E34.22.5.0");var subQ7=makeQuery(id+"F0.imprint","INTERSECT",VERTEX,{"derivedFrom":[subQ6,subQ5]});Q39=makeQuery(id+"F0.imprint","IMPRINT",FACE,{"disambiguationData":[TD([[makeQuery(id+"F0.imprint","IMPRINT",EDGE,{"disambiguationData":[TD([[subQ7,1.0]])],"derivedFrom":subQ6}),-1.0]])]});}
            var Q40;
            Q40=makeQuery(id+"F0.imprint","IMPRINT",FACE,{"disambiguationData":[TD([[makeQuery(id+"F0.imprint","IMPRINT",EDGE,{"derivedFrom":sQuery(id+"F0.wireOp",EDGE,"E33.2.3")}),-1.0]])]});
            var Q41;
            Q41=makeQuery(id+"F0.imprint","IMPRINT",FACE,{"disambiguationData":[TD([[makeQuery(id+"F0.imprint","IMPRINT",EDGE,{"derivedFrom":sQuery(id+"F0.wireOp",EDGE,"E34.7.4.0")}),-1.0]])]});
            var Q42;
            {var subQ0=sQuery(id+"F0.wireOp",EDGE,"E20.MirrorCS");Q42=makeQuery(id+"F0.imprint","IMPRINT",FACE,{"disambiguationData":[TD([[makeQuery(id+"F0.imprint","IMPRINT",EDGE,{"derivedFrom":subQ0}),1.0]])]});}
            var Q43;
            {var subQ0=sQuery(id+"F0.wireOp",EDGE,"E33.2.31");Q43=makeQuery(id+"F0.imprint","IMPRINT",FACE,{"disambiguationData":[TD([[makeQuery(id+"F0.imprint","IMPRINT",EDGE,{"derivedFrom":subQ0}),-1.0]])]});}
            var Q44;
            {var subQ0=sQuery(id+"F0.wireOp",EDGE,"E33.1.31");Q44=makeQuery(id+"F0.imprint","IMPRINT",FACE,{"disambiguationData":[TD([[makeQuery(id+"F0.imprint","IMPRINT",EDGE,{"derivedFrom":subQ0}),-1.0]])]});}
            var Q45;
            {var subQ0=sQuery(id+"F0.wireOp",EDGE,"E34.87.6.0");Q45=makeQuery(id+"F0.imprint","IMPRINT",FACE,{"disambiguationData":[TD([[makeQuery(id+"F0.imprint","IMPRINT",EDGE,{"derivedFrom":subQ0}),-1.0]])]});}
            var Q46;
            {var subQ1=sQuery(id+"F0.wireOp",EDGE,"E33.2.16");Q46=makeQuery(id+"F0.imprint","IMPRINT",FACE,{"disambiguationData":[TD([[makeQuery(id+"F0.imprint","IMPRINT",EDGE,{"derivedFrom":subQ1}),-1.0]])]});}
            var Q47;
            {var subQ0=sQuery(id+"F0.wireOp",EDGE,"E34.37.4.0");Q47=makeQuery(id+"F0.imprint","IMPRINT",FACE,{"disambiguationData":[TD([[makeQuery(id+"F0.imprint","IMPRINT",EDGE,{"derivedFrom":subQ0}),1.0]])]});}
            var Q48;
            {var subQ0=sQuery(id+"F0.wireOp",EDGE,"E34.37.5.0");Q48=makeQuery(id+"F0.imprint","IMPRINT",FACE,{"disambiguationData":[TD([[makeQuery(id+"F0.imprint","IMPRINT",EDGE,{"derivedFrom":subQ0}),1.0]])]});}
            var Q49;
            Q49=makeQuery(id+"F0.imprint","IMPRINT",FACE,{"disambiguationData":[TD([[makeQuery(id+"F0.imprint","IMPRINT",EDGE,{"derivedFrom":sQuery(id+"F0.wireOp",EDGE,"E4")}),-1.0]])]});
            var Q50;
            {var subQ2=sQuery(id+"F0.wireOp",EDGE,"E28.MirrorCS");Q50=makeQuery(id+"F0.imprint","IMPRINT",FACE,{"disambiguationData":[TD([[makeQuery(id+"F0.imprint","IMPRINT",EDGE,{"derivedFrom":subQ2}),1.0]])]});}
            var Q51;
            Q51=makeQuery(id+"F0.imprint","IMPRINT",FACE,{"disambiguationData":[TD([[makeQuery(id+"F0.imprint","IMPRINT",EDGE,{"derivedFrom":sQuery(id+"F0.wireOp",EDGE,"E33.1.3")}),1.0]])]});
            var Q52;
            {var subQ0=sQuery(id+"F0.wireOp",EDGE,"E34.87.4.0");Q52=makeQuery(id+"F0.imprint","IMPRINT",FACE,{"disambiguationData":[TD([[makeQuery(id+"F0.imprint","IMPRINT",EDGE,{"derivedFrom":subQ0}),1.0]])]});}
            var Q53;
            Q53=makeQuery(id+"F0.imprint","IMPRINT",FACE,{"disambiguationData":[TD([[makeQuery(id+"F0.imprint","IMPRINT",EDGE,{"derivedFrom":sQuery(id+"F0.wireOp",EDGE,"E34.7.3.0")}),-1.0]])]});
            var Q54;
            {var subQ0=sQuery(id+"F0.wireOp",EDGE,"E33.2.31");Q54=makeQuery(id+"F0.imprint","IMPRINT",FACE,{"disambiguationData":[TD([[makeQuery(id+"F0.imprint","IMPRINT",EDGE,{"derivedFrom":subQ0}),1.0]])]});}
            var Q55;
            {var subQ0=sQuery(id+"F0.wireOp",EDGE,"E20.MirrorCS");Q55=makeQuery(id+"F0.imprint","IMPRINT",FACE,{"disambiguationData":[TD([[makeQuery(id+"F0.imprint","IMPRINT",EDGE,{"derivedFrom":subQ0}),-1.0]])]});}
            var Q56;
            {var subQ0=sQuery(id+"F0.wireOp",EDGE,"E6");Q56=makeQuery(id+"F0.imprint","IMPRINT",FACE,{"disambiguationData":[TD([[makeQuery(id+"F0.imprint","IMPRINT",EDGE,{"derivedFrom":subQ0}),-1.0]])]});}
            var Q57;
            Q57=makeQuery(id+"F0.imprint","IMPRINT",FACE,{"disambiguationData":[TD([[makeQuery(id+"F0.imprint","IMPRINT",EDGE,{"derivedFrom":sQuery(id+"F0.wireOp",EDGE,"E34.7.5.0")}),-1.0]])]});
            var Q58;
            {var subQ0=sQuery(id+"F0.wireOp",EDGE,"E33.1.28");Q58=makeQuery(id+"F0.imprint","IMPRINT",FACE,{"disambiguationData":[TD([[makeQuery(id+"F0.imprint","IMPRINT",EDGE,{"derivedFrom":subQ0}),-1.0]])]});}
            var Q59;
            {var subQ0=sQuery(id+"F0.wireOp",EDGE,"E33.1.31");Q59=makeQuery(id+"F0.imprint","IMPRINT",FACE,{"disambiguationData":[TD([[makeQuery(id+"F0.imprint","IMPRINT",EDGE,{"derivedFrom":subQ0}),1.0]])]});}
            var Q60;
            Q60=makeQuery(id+"F0.imprint","IMPRINT",FACE,{"disambiguationData":[TD([[makeQuery(id+"F0.imprint","IMPRINT",EDGE,{"derivedFrom":sQuery(id+"F0.wireOp",EDGE,"E34.7.6.0")}),-1.0]])]});
            var Q61;
            {var subQ0=sQuery(id+"F0.wireOp",EDGE,"E34.37.6.0");Q61=makeQuery(id+"F0.imprint","IMPRINT",FACE,{"disambiguationData":[TD([[makeQuery(id+"F0.imprint","IMPRINT",EDGE,{"derivedFrom":subQ0}),1.0]])]});}
            var Q62;
            Q62=makeQuery(id+"F0.imprint","IMPRINT",FACE,{"disambiguationData":[TD([[makeQuery(id+"F0.imprint","IMPRINT",EDGE,{"derivedFrom":sQuery(id+"F0.wireOp",EDGE,"E4")}),1.0]])]});
            var Q63;
            {var subQ1=sQuery(id+"F0.wireOp",EDGE,"E34.61.4.0");var subQ3=sQuery(id+"F0.wireOp",EDGE,"E34.105.5.0");var subQ4=makeQuery(id+"F0.imprint","INTERSECT",VERTEX,{"derivedFrom":[subQ1,subQ3]});Q63=makeQuery(id+"F0.imprint","IMPRINT",FACE,{"disambiguationData":[TD([[makeQuery(id+"F0.imprint","IMPRINT",EDGE,{"disambiguationData":[TD([[subQ4,1.0]])],"derivedFrom":subQ3}),-1.0]])]});}
            var Q64;
            {var subQ1=sQuery(id+"F0.wireOp",EDGE,"E28.MirrorCS");Q64=makeQuery(id+"F0.imprint","IMPRINT",FACE,{"disambiguationData":[TD([[makeQuery(id+"F0.imprint","IMPRINT",EDGE,{"derivedFrom":subQ1}),-1.0]])]});}
            var Q65;
            {var subQ0=sQuery(id+"F0.wireOp",EDGE,"E34.87.3.0");Q65=makeQuery(id+"F0.imprint","IMPRINT",FACE,{"disambiguationData":[TD([[makeQuery(id+"F0.imprint","IMPRINT",EDGE,{"derivedFrom":subQ0}),1.0]])]});}
            var Q66;
            Q66=makeQuery(id+"F0.imprint","IMPRINT",FACE,{"disambiguationData":[TD([[makeQuery(id+"F0.imprint","IMPRINT",EDGE,{"derivedFrom":sQuery(id+"F0.wireOp",EDGE,"E33.2.3")}),1.0]])]});
            var Q67;
            {var subQ1=sQuery(id+"F0.wireOp",EDGE,"E33.1.5");Q67=makeQuery(id+"F0.imprint","IMPRINT",FACE,{"disambiguationData":[TD([[makeQuery(id+"F0.imprint","IMPRINT",EDGE,{"derivedFrom":subQ1}),-1.0]])]});}
            var Q68;
            Q68=makeQuery(id+"F0.imprint","IMPRINT",FACE,{"disambiguationData":[TD([[makeQuery(id+"F0.imprint","IMPRINT",EDGE,{"derivedFrom":sQuery(id+"F0.wireOp",EDGE,"E34.7.3.0")}),1.0]])]});
            var Q69;
            {var subQ1=sQuery(id+"F0.wireOp",EDGE,"E34.61.3.0");var subQ3=sQuery(id+"F0.wireOp",EDGE,"E34.105.4.0");var subQ4=makeQuery(id+"F0.imprint","INTERSECT",VERTEX,{"derivedFrom":[subQ1,subQ3]});Q69=makeQuery(id+"F0.imprint","IMPRINT",FACE,{"disambiguationData":[TD([[makeQuery(id+"F0.imprint","IMPRINT",EDGE,{"disambiguationData":[TD([[subQ4,1.0]])],"derivedFrom":subQ3}),-1.0]])]});}
            var Q70;
            {var subQ1=sQuery(id+"F0.wireOp",EDGE,"E7");var subQ3=sQuery(id+"F0.wireOp",EDGE,"E33.1.37");var subQ4=makeQuery(id+"F0.imprint","INTERSECT",VERTEX,{"derivedFrom":[subQ1,subQ3]});Q70=makeQuery(id+"F0.imprint","IMPRINT",FACE,{"disambiguationData":[TD([[makeQuery(id+"F0.imprint","IMPRINT",EDGE,{"disambiguationData":[TD([[subQ4,1.0]])],"derivedFrom":subQ3}),-1.0]])]});}
            var Q71;
            {var subQ1=sQuery(id+"F0.wireOp",EDGE,"E33.1.22");var subQ3=sQuery(id+"F0.wireOp",EDGE,"E33.2.37");var subQ4=makeQuery(id+"F0.imprint","INTERSECT",VERTEX,{"derivedFrom":[subQ1,subQ3]});Q71=makeQuery(id+"F0.imprint","IMPRINT",FACE,{"disambiguationData":[TD([[makeQuery(id+"F0.imprint","IMPRINT",EDGE,{"disambiguationData":[TD([[subQ4,1.0]])],"derivedFrom":subQ3}),-1.0]])]});}
            var Q72;
            {var subQ0=sQuery(id+"F0.wireOp",EDGE,"E34.87.5.0");Q72=makeQuery(id+"F0.imprint","IMPRINT",FACE,{"disambiguationData":[TD([[makeQuery(id+"F0.imprint","IMPRINT",EDGE,{"derivedFrom":subQ0}),1.0]])]});}
            var Q73;
            Q73=makeQuery(id+"F0.imprint","IMPRINT",FACE,{"disambiguationData":[TD([[makeQuery(id+"F0.imprint","IMPRINT",EDGE,{"derivedFrom":sQuery(id+"F0.wireOp",EDGE,"E34.7.5.0")}),1.0]])]});
            var Q74;
            {var subQ0=sQuery(id+"F0.wireOp",EDGE,"E6");Q74=makeQuery(id+"F0.imprint","IMPRINT",FACE,{"disambiguationData":[TD([[makeQuery(id+"F0.imprint","IMPRINT",EDGE,{"derivedFrom":subQ0}),1.0]])]});}
            var Q75;
            Q75=makeQuery(id+"F0.imprint","IMPRINT",FACE,{"disambiguationData":[TD([[makeQuery(id+"F0.imprint","IMPRINT",EDGE,{"derivedFrom":sQuery(id+"F0.wireOp",EDGE,"E34.7.4.0")}),1.0]])]});
            var Q76;
            {var subQ1=sQuery(id+"F0.wireOp",EDGE,"E34.61.5.0");var subQ3=sQuery(id+"F0.wireOp",EDGE,"E34.105.6.0");var subQ4=makeQuery(id+"F0.imprint","INTERSECT",VERTEX,{"derivedFrom":[subQ1,subQ3]});Q76=makeQuery(id+"F0.imprint","IMPRINT",FACE,{"disambiguationData":[TD([[makeQuery(id+"F0.imprint","IMPRINT",EDGE,{"disambiguationData":[TD([[subQ4,1.0]])],"derivedFrom":subQ3}),-1.0]])]});}
            var Q77;
            {var subQ0=sQuery(id+"F0.wireOp",EDGE,"E33.1.29");var subQ1=sQuery(id+"F0.wireOp",EDGE,"E1");var subQ2=makeQuery(id+"F0.imprint","INTERSECT",VERTEX,{"derivedFrom":[subQ1,subQ0]});Q77=makeQuery(id+"F0.imprint","IMPRINT",FACE,{"disambiguationData":[TD([[makeQuery(id+"F0.imprint","IMPRINT",EDGE,{"disambiguationData":[TD([[subQ2,-1.0]])],"derivedFrom":subQ1}),-1.0]])]});}
            var Q78;
            {var subQ1=sQuery(id+"F0.wireOp",EDGE,"E33.2.22");var subQ3=sQuery(id+"F0.wireOp",EDGE,"E34.105.3.0");var subQ4=makeQuery(id+"F0.imprint","INTERSECT",VERTEX,{"derivedFrom":[subQ1,subQ3]});Q78=makeQuery(id+"F0.imprint","IMPRINT",FACE,{"disambiguationData":[TD([[makeQuery(id+"F0.imprint","IMPRINT",EDGE,{"disambiguationData":[TD([[subQ4,1.0]])],"derivedFrom":subQ3}),-1.0]])]});}
            var Q79;
            {var subQ1=sQuery(id+"F0.wireOp",EDGE,"E18.MirrorCS");var subQ3=sQuery(id+"F0.wireOp",EDGE,"E34.105.7.0");var subQ4=makeQuery(id+"F0.imprint","INTERSECT",VERTEX,{"derivedFrom":[subQ1,subQ3]});Q79=makeQuery(id+"F0.imprint","IMPRINT",FACE,{"disambiguationData":[TD([[makeQuery(id+"F0.imprint","IMPRINT",EDGE,{"disambiguationData":[TD([[subQ4,-1.0]])],"derivedFrom":subQ3}),-1.0]])]});}
            extrude(context, id + "F1", {"entities" : qUnion([Q0, Q1, Q2, Q3, Q4, Q5, Q6, Q7, Q8, Q9, Q10, Q11, Q12, Q13, Q14, Q15, Q16, Q17, Q18, Q19, Q20, Q21, Q22, Q23, Q24, Q25, Q26, Q27, Q28, Q29, Q30, Q31, Q32, Q33, Q34, Q35, Q36, Q37, Q38, Q39, Q40, Q41, Q42, Q43, Q44, Q45, Q46, Q47, Q48, Q49, Q50, Q51, Q52, Q53, Q54, Q55, Q56, Q57, Q58, Q59, Q60, Q61, Q62, Q63, Q64, Q65, Q66, Q67, Q68, Q69, Q70, Q71, Q72, Q73, Q74, Q75, Q76, Q77, Q78, Q79]), "depth" : 6 * mm, "offsetDistance" : 25 * mm});
        }
    });
